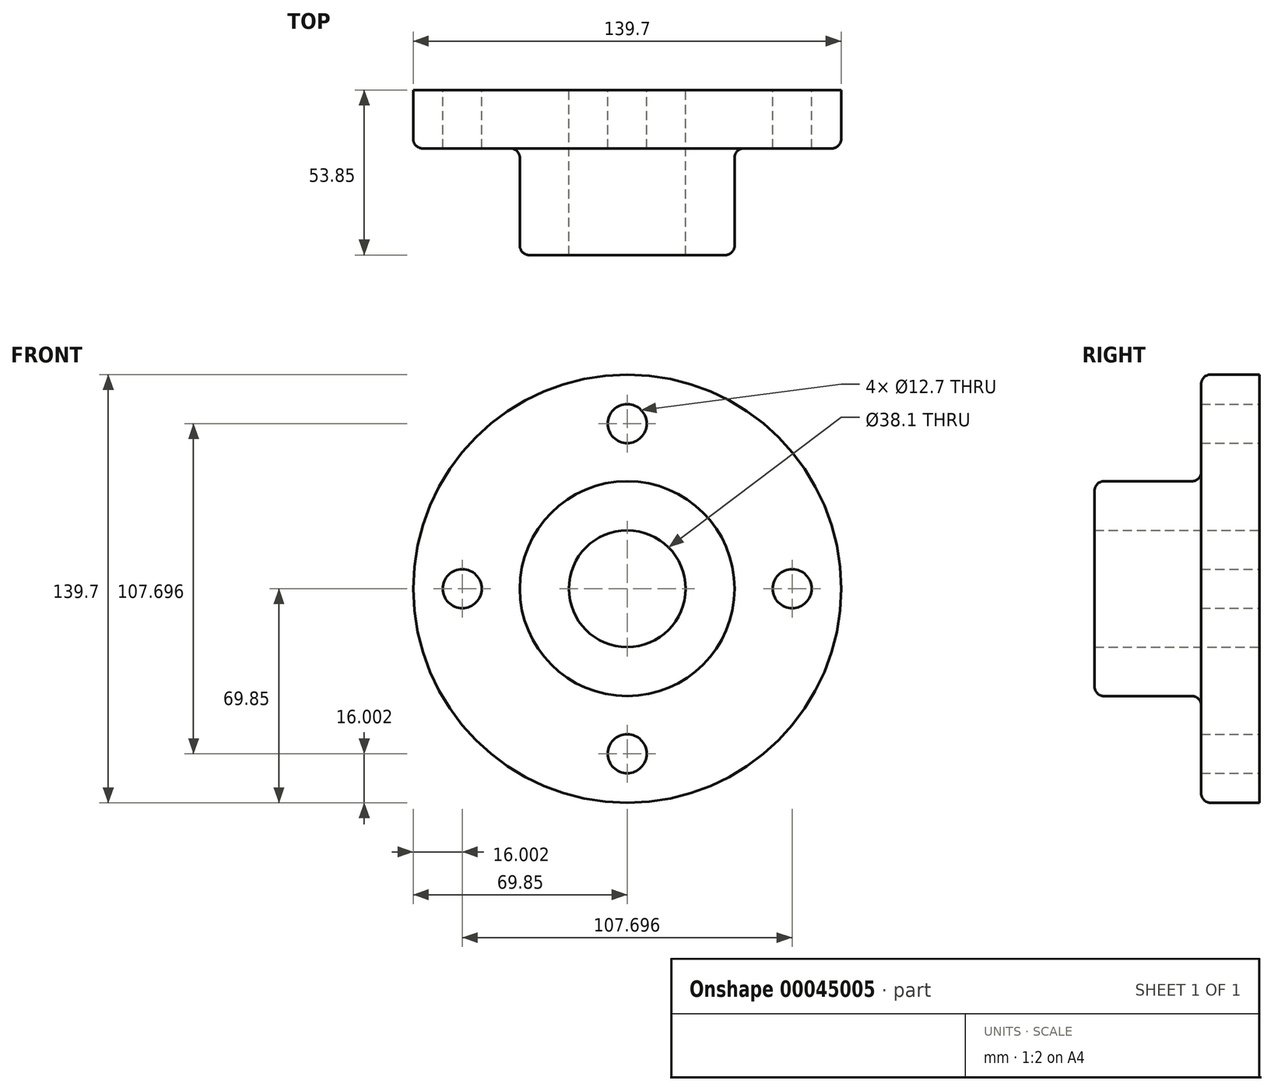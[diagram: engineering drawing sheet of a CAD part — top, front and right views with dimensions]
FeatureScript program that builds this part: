
annotation { "Feature Type Name" : "Feature", "Feature Type Description" : "" }
export const myFeature = defineFeature(function(context is Context, id is Id, definition is map)
    precondition{}
    {
        {
            var Q0;
            Q0=qCreatedBy(makeId("Front.planeOp"),FACE);
            var sketch = newSketch(context, id + "F0", { "sketchPlane" : qUnion([Q0])});
            skCircle(sketch, "E0", {"center": v(0, 0) * mm, "radius": 69.85 * mm});
            skSolve(sketch);
        }
        {
            var Q0;
            Q0 = qSketchRegion(id + "F0", true);
            extrude(context, id + "F1", {"entities" : qUnion([Q0]), "depth" : 19.05 * mm});
        }
        {
            var Q0;
            Q0=qCreatedBy(makeId("Front.planeOp"),FACE);
            var sketch = newSketch(context, id + "F2", { "sketchPlane" : qUnion([Q0])});
            skCircle(sketch, "E1", {"center": v(0, 0) * mm, "radius": 35.05 * mm});
            skSolve(sketch);
        }
        {
            var Q0;
            Q0 = qSketchRegion(id + "F2", true);
            extrude(context, id + "F3", {"entities" : qUnion([Q0]), "operationType" : NewBodyOperationType.ADD, "depth" : 53.85 * mm});
        }
        {
            var Q0;
            Q0=qCreatedBy(makeId("Front.planeOp"),FACE);
            var sketch = newSketch(context, id + "F4", { "sketchPlane" : qUnion([Q0])});
            skCircle(sketch, "E2", {"center": v(0, 0) * mm, "radius": 19.05 * mm});
            skSolve(sketch);
        }
        {
            var Q0;
            Q0 = qSketchRegion(id + "F4", true);
            extrude(context, id + "F5", {"entities" : qUnion([Q0]), "operationType" : NewBodyOperationType.REMOVE, "endBound" : BoundingType.THROUGH_ALL, "depth" : 25.4 * mm});
        }
        {
            var Q0;
            Q0=qCreatedBy(makeId("Front.planeOp"),FACE);
            var sketch = newSketch(context, id + "F6", { "sketchPlane" : qUnion([Q0])});
            skCircle(sketch, "E3", {"center": v(0, 0) * mm, "radius": 53.85 * mm, "construction": true});
            skCircle(sketch, "E4", {"center": v(0, 53.85) * mm, "radius": 6.35 * mm});
            skCircle(sketch, "E5.1.0", {"center": v(-53.85, 0) * mm, "radius": 6.35 * mm});
            skCircle(sketch, "E5.2.0", {"center": v(0, -53.85) * mm, "radius": 6.35 * mm});
            skCircle(sketch, "E5.3.0", {"center": v(53.85, 0) * mm, "radius": 6.35 * mm});
            skSolve(sketch);
        }
        {
            var Q0;
            Q0=makeQuery(id+"F6.imprint","IMPRINT",FACE,{"disambiguationData":[TD([[makeQuery(id+"F6.imprint","IMPRINT",EDGE,{"derivedFrom":sQuery(id+"F6.wireOp",EDGE,"E5.3.0")}),1.0]])]});
            var Q1;
            Q1=makeQuery(id+"F6.imprint","IMPRINT",FACE,{"disambiguationData":[TD([[makeQuery(id+"F6.imprint","IMPRINT",EDGE,{"derivedFrom":sQuery(id+"F6.wireOp",EDGE,"E4")}),1.0]])]});
            var Q2;
            Q2=makeQuery(id+"F6.imprint","IMPRINT",FACE,{"disambiguationData":[TD([[makeQuery(id+"F6.imprint","IMPRINT",EDGE,{"derivedFrom":sQuery(id+"F6.wireOp",EDGE,"E5.1.0")}),1.0]])]});
            var Q3;
            Q3=makeQuery(id+"F6.imprint","IMPRINT",FACE,{"disambiguationData":[TD([[makeQuery(id+"F6.imprint","IMPRINT",EDGE,{"derivedFrom":sQuery(id+"F6.wireOp",EDGE,"E5.2.0")}),1.0]])]});
            extrude(context, id + "F7", {"entities" : qUnion([Q0, Q1, Q2, Q3]), "operationType" : NewBodyOperationType.REMOVE, "endBound" : BoundingType.THROUGH_ALL, "depth" : 25.4 * mm});
        }
        {
            var Q0;
            Q0=makeQuery(id+"F1.opExtrude","CAP_EDGE",EDGE,{"disambiguationData":[OSD([sQuery(id+"F0.wireOp",EDGE,"E0")])],"isStart":false});
            var Q1;
            Q1=makeQuery(id+"F3.boolean.opBoolean","INTERSECT",EDGE,{"derivedFrom":[makeQuery(id+"F1.opExtrude","CAP_FACE",FACE,{"disambiguationData":[OSD([sQuery(id+"F0.wireOp",EDGE,"E0")])],"isStart":false}),makeQuery(id+"F3.opExtrude","SWEPT_FACE",FACE,{"disambiguationData":[OSD([sQuery(id+"F2.wireOp",EDGE,"E1")])]})]});
            var Q2;
            Q2=makeQuery(id+"F3.opExtrude","CAP_EDGE",EDGE,{"disambiguationData":[OSD([sQuery(id+"F2.wireOp",EDGE,"E1")])],"isStart":false});
            fillet(context, id + "F8", {"entities" : qUnion([Q0, Q1, Q2]), "radius" : 3.05 * mm, "tangentPropagation" : true, "allowEdgeOverflow" : false});
        }
    });
